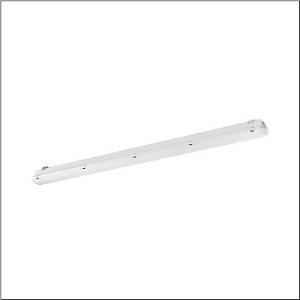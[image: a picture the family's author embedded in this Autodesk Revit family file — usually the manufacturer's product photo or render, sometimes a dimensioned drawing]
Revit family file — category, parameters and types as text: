
# Revit family: monsun_11xtreme_mo_51fe10dp460m
name_source: partatom
category: Lighting Fixtures
units: mm (PartAtom-declared; Revit-internal decimal feet)

## family parameters
Cut with Voids When Loaded = No
Host = Face
Light Source = No
Part Type = Normal
Room Calculation Point = No
Round Connector Dimension = Use Diameter
Shared = No

## types (1)
- --- (1 x LED, 6370 lm, 34.5 W, 4000K)
    Apparent Load = 35 VA
    CIE Flux Codes = 47 77 93 94 100
    Color Rendering = 80
    Color Temperature = 4000K
    Default Elevation = 1800 mm
    Description = Monsun 11Xtreme MO, damp-proof luminaire, chain hanger, primary optical cover: enclosure, of PMMA, light emission: direct distribution, primary light characteristic: symmetric, installation type: suspended mounting, surface-mounted, horizontal mounting, vertical mounting, LED, rated luminous flux: 6.370lm, luminous efficacy: 185lm/W, light colour: 840, colour temperature: 4000K, control gear: DALI 2, with terminal, 5-pole, max. 2.5mm², mains connection: 220..240V, AC, 50/60Hz, rated input power: 35W, luminaire housing, of glass-fibre reinforced polyester, uncoated, bright grey, incl. chain hanger, length: 1.590mm, width: 90mm, height: 88mm, clip for enclosure, of stainless steel (V2A), ceiling mounting element, of stainless steel (V2A), chain hanger, of stainless steel (V2A), protection rating (complete): IP66, insulation class (complete): insulation class I (protective earthing), certification: CE, ENEC, VDE, UKCA, protection symbol: D, impact resistance: IK04, permissible operating ambient temperature: -40..+45°C, standard: EN 50419, EN 60598-2-1, contact your sales advisor before using the luminaires in applications with unclear chemical exposure, large temperature fluctuations or condensation-forming humidity, LABS conformity tested according to VDMA 24364:2018-05, no direct snow, no direct sun, no direct rain, for indoor or canopied outdoor use, corresponds to IFS (International Featured Standards) requirements for safety and quality in the food industry, packaging unit: 1 piece
    Height = 88 mm
    Lamp = 1 x LED
    Lamp Light Flux = 6370 lm
    Lamp Power = 34.5 W
    Lamp count = 1
    Length = 1590 mm
    Luminous efficacy = 185 lm/W
    Manufacturer = Siteco
    ModVariant = No
    Model = 51FE10DP460M
    Mounting Place = Ceiling
    Mounting Type = Surface mounted
    Number of Poles = 1
    OnlyDefault = Yes
    Power Factor = 1
    Product Name = Monsun 11Xtreme MO
    Product group = damp-proof luminaire
    ProductGroupID = 300
    Protection Class = Protection class I
    Protection Degree = IP 66
    RLX_Detail_Level = 1
    RLX_Emergency_Light_Flux = 0 lm
    RLX_Emergency_Type = 0
    RLX_Emergency_Type_DB = No
    RlxData = <blob elided: 87089 chars, md5=0beee7a9>
    Socket = socket
    Standby Power = 0 W
    System Light Flux = 6370 lm
    System Power = 35 W
    Type Comments = factory setting: luminous flux: 100 % | dim-lin: 254 | 231 mA
    Type Image = l_1349234.jpg
    URL = http://relux.com
    VarID = @adj_033601
    Voltage = 0 V
    Weight = 0.00 kg
    Width = 90 mm

## geometry (parser evidence)
native form markers: Blend x4, Sweep x12
no freeform markers — native parametric forms only
